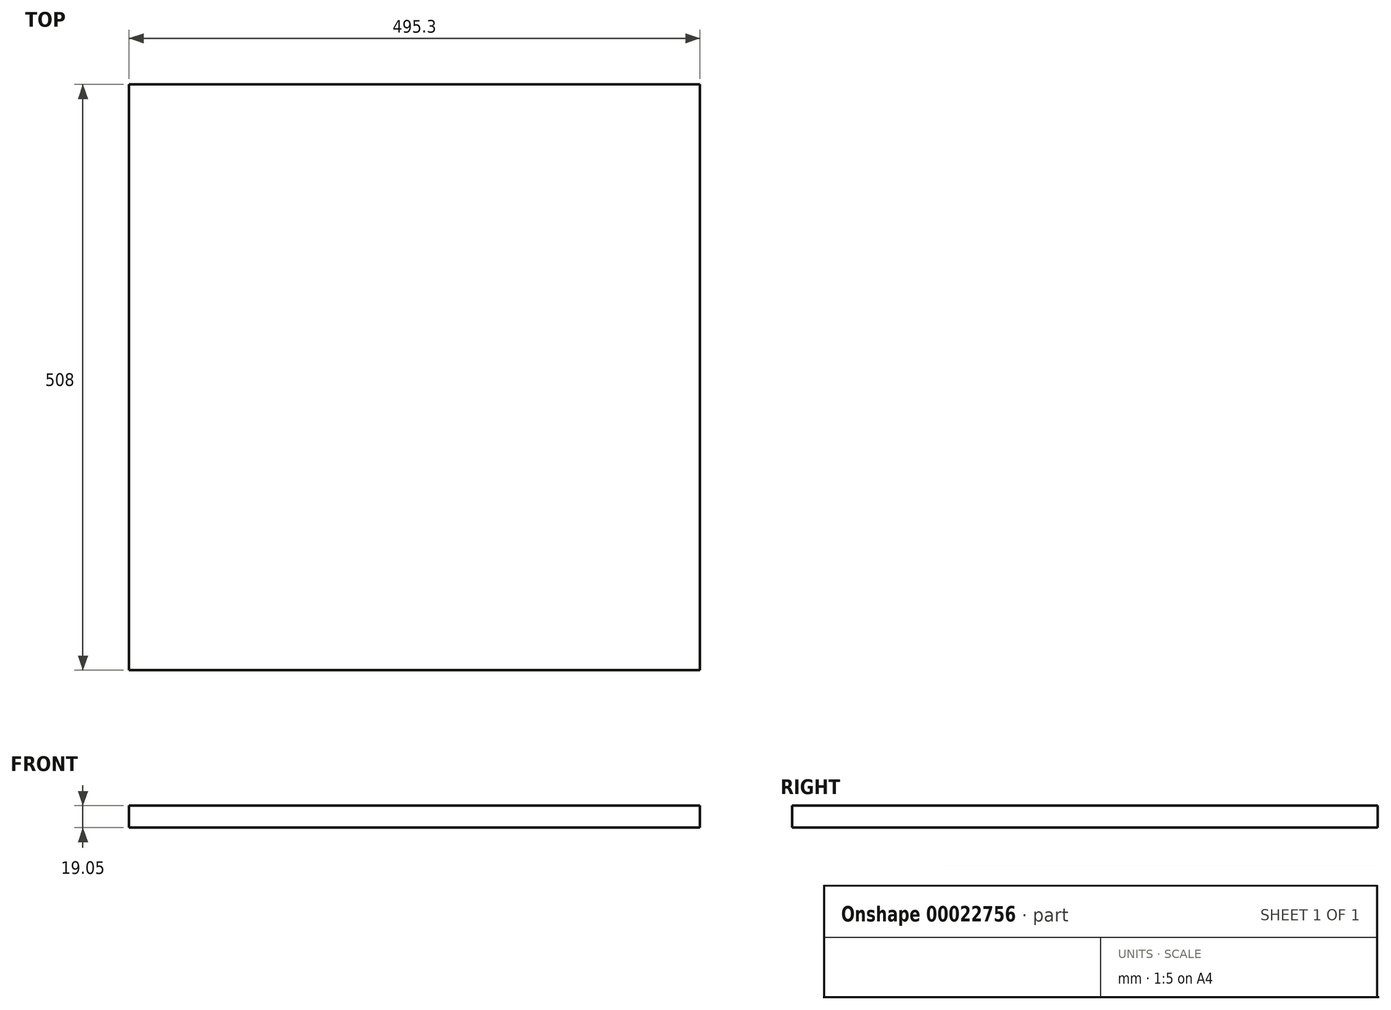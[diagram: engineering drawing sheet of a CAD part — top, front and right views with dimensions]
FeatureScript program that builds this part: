
annotation { "Feature Type Name" : "Feature", "Feature Type Description" : "" }
export const myFeature = defineFeature(function(context is Context, id is Id, definition is map)
    precondition{}
    {
        {
            var Q0;
            Q0=qCreatedBy(makeId("Top.planeOp"),FACE);
            var sketch = newSketch(context, id + "F0", { "sketchPlane" : qUnion([Q0])});
            skLineSegment(sketch, "E0.rect.bottom", {"start": v(222.25, 254) * mm, "end": v(-222.25, 254) * mm});
            skLineSegment(sketch, "E0.rect.top", {"start": v(222.25, -254) * mm, "end": v(-222.25, -254) * mm});
            skLineSegment(sketch, "E0.rect.left", {"start": v(222.25, 254) * mm, "end": v(222.25, -254) * mm});
            skLineSegment(sketch, "E0.rect.right", {"start": v(-222.25, 254) * mm, "end": v(-222.25, -254) * mm});
            skPoint(sketch, "E0.rect.middle", {"position": v(0, 0) * mm});
            skSolve(sketch);
        }
        {
            var Q0;
            Q0=makeQuery(id+"F0.imprint","IMPRINT",FACE,{"disambiguationData":[TD([[makeQuery(id+"F0.imprint","IMPRINT",EDGE,{"derivedFrom":sQuery(id+"F0.wireOp",EDGE,"E0.rect.bottom")}),1.0]])]});
            extrude(context, id + "F1", {"entities" : qUnion([Q0]), "depth" : 19.05 * mm});
        }
        {
            var Q0;
            Q0=makeQuery(id+"F1.opExtrude","SWEPT_FACE",FACE,{"disambiguationData":[OSD([sQuery(id+"F0.wireOp",EDGE,"E0.rect.right")])]});
            var sketch = newSketch(context, id + "F2", { "sketchPlane" : qUnion([Q0])});
            skLineSegment(sketch, "E1.bottom", {"start": v(-254, 0) * mm, "end": v(254, 0) * mm});
            skLineSegment(sketch, "E1.top", {"start": v(-254, 19.05) * mm, "end": v(254, 19.05) * mm});
            skLineSegment(sketch, "E1.left", {"start": v(-254, 0) * mm, "end": v(-254, 19.05) * mm});
            skLineSegment(sketch, "E1.right", {"start": v(254, 0) * mm, "end": v(254, 19.05) * mm});
            skSolve(sketch);
        }
        {
            var Q0;
            Q0 = qSketchRegion(id + "F2", true);
            extrude(context, id + "F3", {"entities" : qUnion([Q0]), "operationType" : NewBodyOperationType.ADD, "depth" : 50.8 * mm});
        }
    });
